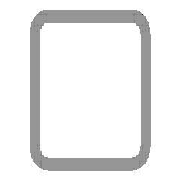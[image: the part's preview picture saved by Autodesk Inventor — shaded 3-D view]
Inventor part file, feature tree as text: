
AUTODESK INVENTOR PART (.ipt)
format: ipt  version: 2022 (Build 260153000, 153)  size: 135,168 bytes
history: native  units: mm (DEFAULTED — no unit token found)
features: other x4, sketch x3, plane x1
ambient origin geometry x8: Origin, YZ Plane, XZ Plane, XY Plane, X Axis, Y Axis, Z Axis, Center Point
bodies: Solid1 (feature_tree), Body (feature_tree)
feature tree (8):
  parser-record x1  (decoder bookkeeping rows leaked as tree rows — omitted from the tree; the rows remain in map.json)
  other  "Driven Length"
  other  "Start Plane"
  other  "End Plane"
  sketch  "Sketch"  dims[d7=7.5mm d10=40.0mm d11=40.0mm d12=5.0mm d13=-0.0mm d14=180.0mm d15=20.0mm d16=20.0mm d17=90.0deg d18=180.0mm]
  sketch  "Sketch3"  dims[d3=180.0mm]
  plane  "Work Plane3"
  sketch  "Sketch4"  dims[d4=0.0mm]
